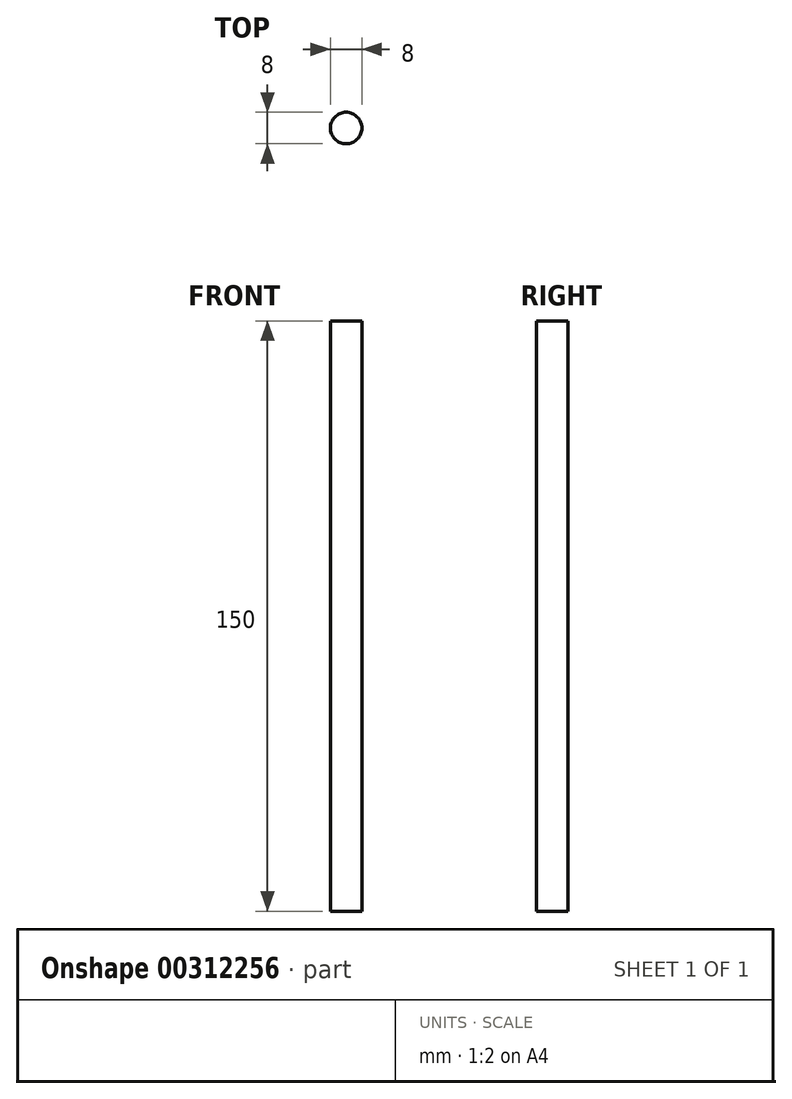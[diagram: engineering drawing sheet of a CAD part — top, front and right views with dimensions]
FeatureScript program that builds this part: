
annotation { "Feature Type Name" : "Feature", "Feature Type Description" : "" }
export const myFeature = defineFeature(function(context is Context, id is Id, definition is map)
    precondition{}
    {
        {
            var Q0;
            Q0=qCreatedBy(makeId("Top.planeOp"),FACE);
            var sketch = newSketch(context, id + "F0", { "sketchPlane" : qUnion([Q0])});
            skCircle(sketch, "E0", {"center": v(0, 0) * mm, "radius": 4 * mm});
            skSolve(sketch);
        }
        {
            var Q0;
            Q0=makeQuery(id+"F0.imprint","IMPRINT",FACE,{"disambiguationData":[TD([[makeQuery(id+"F0.imprint","IMPRINT",EDGE,{"derivedFrom":sQuery(id+"F0.wireOp",EDGE,"E0")}),1.0]])]});
            extrude(context, id + "F1", {"entities" : qUnion([Q0]), "depth" : 150 * mm});
        }
    });
